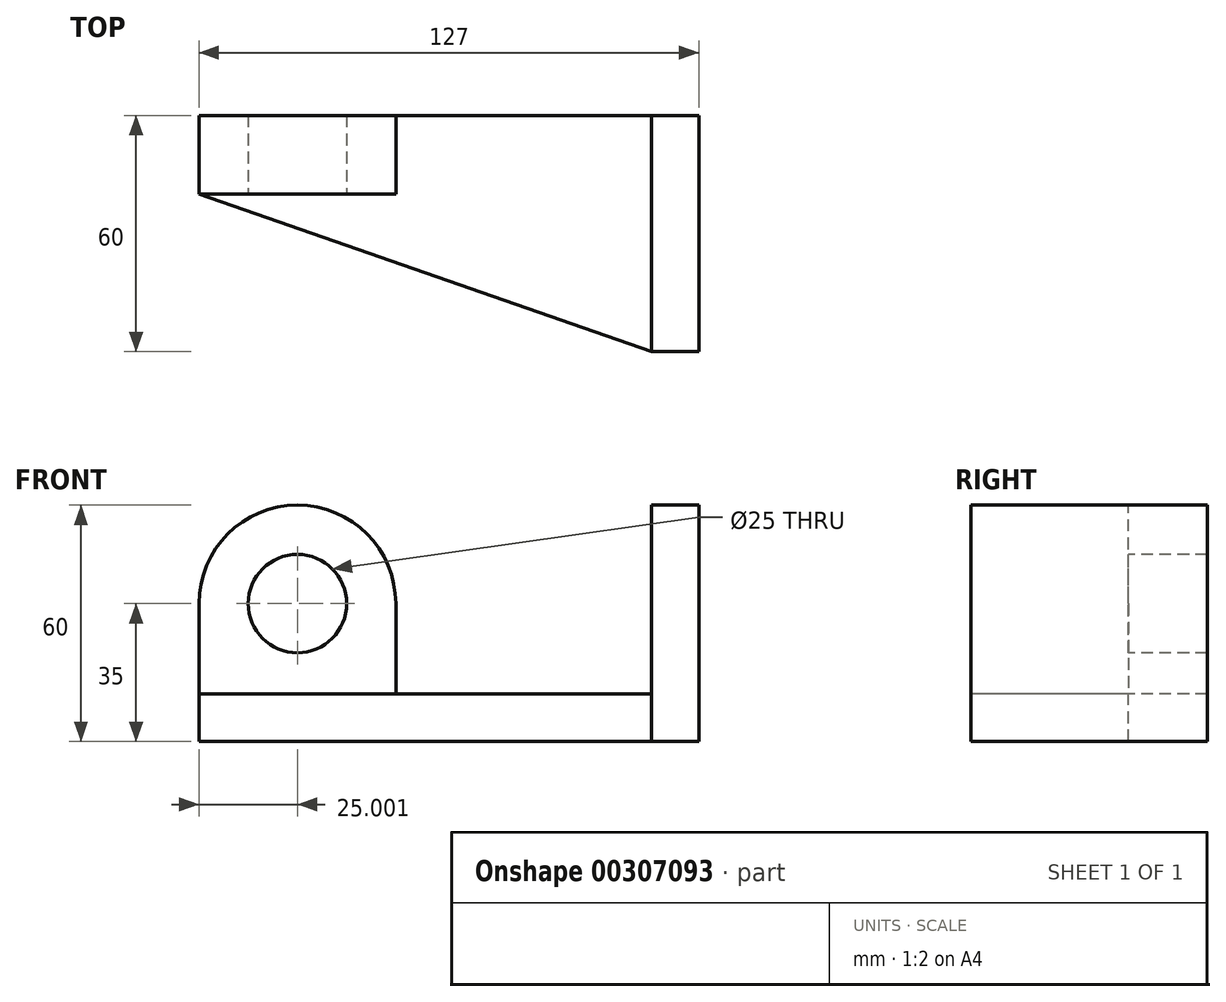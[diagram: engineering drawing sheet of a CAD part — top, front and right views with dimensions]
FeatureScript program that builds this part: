
annotation { "Feature Type Name" : "Feature", "Feature Type Description" : "" }
export const myFeature = defineFeature(function(context is Context, id is Id, definition is map)
    precondition{}
    {
        {
            var Q0;
            Q0=qCreatedBy(makeId("Top.planeOp"),FACE);
            var sketch = newSketch(context, id + "F0", { "sketchPlane" : qUnion([Q0])});
            skLineSegment(sketch, "E0.bottom", {"start": v(-57.94, 26.08) * mm, "end": v(57.06, 26.08) * mm});
            skLineSegment(sketch, "E0.top", {"start": v(-57.94, -33.92) * mm, "end": v(57.06, -33.92) * mm});
            skLineSegment(sketch, "E0.left", {"start": v(-57.94, 26.08) * mm, "end": v(-57.94, -33.92) * mm});
            skLineSegment(sketch, "E0.right", {"start": v(57.06, 26.08) * mm, "end": v(57.06, -33.92) * mm});
            skLineSegment(sketch, "E1.bottom", {"start": v(57.06, 26.08) * mm, "end": v(69.06, 26.08) * mm});
            skLineSegment(sketch, "E1.top", {"start": v(57.06, -33.92) * mm, "end": v(69.06, -33.92) * mm});
            skLineSegment(sketch, "E1.right", {"start": v(69.06, 26.08) * mm, "end": v(69.06, -33.92) * mm});
            skSolve(sketch);
        }
        {
            var Q0;
            Q0=makeQuery(id+"F0.imprint","IMPRINT",FACE,{"disambiguationData":[TD([[makeQuery(id+"F0.imprint","IMPRINT",EDGE,{"derivedFrom":sQuery(id+"F0.wireOp",EDGE,"E0.bottom")}),-1.0]])]});
            extrude(context, id + "F1", {"entities" : qUnion([Q0]), "depth" : 12 * mm});
        }
        {
            var Q0;
            Q0=makeQuery(id+"F0.imprint","IMPRINT",FACE,{"disambiguationData":[TD([[makeQuery(id+"F0.imprint","IMPRINT",EDGE,{"derivedFrom":sQuery(id+"F0.wireOp",EDGE,"E1.bottom")}),-1.0]])]});
            extrude(context, id + "F2", {"entities" : qUnion([Q0]), "operationType" : NewBodyOperationType.ADD, "depth" : 60 * mm});
        }
        {
            var Q0;
            Q0=makeQuery(id+"F1.opExtrude","CAP_FACE",FACE,{"disambiguationData":[OSD([sQuery(id+"F0.wireOp",EDGE,"E0.bottom"),sQuery(id+"F0.wireOp",EDGE,"E0.top"),sQuery(id+"F0.wireOp",EDGE,"E0.left"),sQuery(id+"F0.wireOp",EDGE,"E0.right")])],"isStart":false});
            var sketch = newSketch(context, id + "F3", { "sketchPlane" : qUnion([Q0])});
            skLineSegment(sketch, "E2", {"start": v(-57.94, 26.08) * mm, "end": v(-57.94, 6.08) * mm});
            skLineSegment(sketch, "E3", {"start": v(-57.94, 6.08) * mm, "end": v(57.06, -33.92) * mm});
            skLineSegment(sketch, "E4", {"start": v(57.06, -33.92) * mm, "end": v(-57.94, -33.92) * mm});
            skLineSegment(sketch, "E5", {"start": v(-57.94, -33.92) * mm, "end": v(-57.94, 6.08) * mm});
            skSolve(sketch);
        }
        {
            var Q0;
            Q0=makeQuery(id+"F3.imprint","IMPRINT",FACE,{"disambiguationData":[TD([[makeQuery(id+"F3.imprint","IMPRINT",EDGE,{"derivedFrom":sQuery(id+"F3.wireOp",EDGE,"E3")}),-1.0]])]});
            extrude(context, id + "F4", {"entities" : qUnion([Q0]), "operationType" : NewBodyOperationType.REMOVE, "oppositeDirection" : true, "depth" : 25 * mm});
        }
        {
            var Q0;
            Q0=makeQuery(id+"F1.opExtrude","CAP_FACE",FACE,{"disambiguationData":[OSD([sQuery(id+"F0.wireOp",EDGE,"E0.bottom"),sQuery(id+"F0.wireOp",EDGE,"E0.top"),sQuery(id+"F0.wireOp",EDGE,"E0.left"),sQuery(id+"F0.wireOp",EDGE,"E0.right")])],"isStart":false});
            var sketch = newSketch(context, id + "F5", { "sketchPlane" : qUnion([Q0])});
            skLineSegment(sketch, "E6.bottom", {"start": v(-57.94, 26.08) * mm, "end": v(-57.94, 26.08) * mm});
            skLineSegment(sketch, "E6.top", {"start": v(-57.94, 6.08) * mm, "end": v(-57.94, 6.08) * mm});
            skLineSegment(sketch, "E6.left", {"start": v(-57.94, 26.08) * mm, "end": v(-57.94, 6.08) * mm});
            skLineSegment(sketch, "E6.right", {"start": v(-57.94, 26.08) * mm, "end": v(-57.94, 6.08) * mm});
            skLineSegment(sketch, "E7.bottom", {"start": v(-57.94, 26.08) * mm, "end": v(-7.94, 26.08) * mm});
            skLineSegment(sketch, "E7.top", {"start": v(-57.94, 6.08) * mm, "end": v(-7.94, 6.08) * mm});
            skLineSegment(sketch, "E7.right", {"start": v(-7.94, 26.08) * mm, "end": v(-7.94, 6.08) * mm});
            skSolve(sketch);
        }
        {
            var Q0;
            Q0=makeQuery(id+"F5.imprint","IMPRINT",FACE,{"disambiguationData":[TD([[makeQuery(id+"F5.imprint","IMPRINT",EDGE,{"derivedFrom":sQuery(id+"F5.wireOp",EDGE,"E7.bottom")}),-1.0]])]});
            extrude(context, id + "F6", {"entities" : qUnion([Q0]), "operationType" : NewBodyOperationType.ADD, "depth" : 48 * mm});
        }
        {
            var Q0;
            Q0=makeQuery(id+"F6.opExtrude","SWEPT_FACE",FACE,{"disambiguationData":[OSD([sQuery(id+"F5.wireOp",EDGE,"E7.top")])]});
            var sketch = newSketch(context, id + "F7", { "sketchPlane" : qUnion([Q0])});
            skLineSegment(sketch, "E8", {"start": v(-57.94, 12) * mm, "end": v(-57.94, 35) * mm});
            skArc(sketch, "E9", {"start": v(-7.94, 35) * mm, "mid": v(-32.94, 60) * mm, "end": v(-57.94, 35) * mm});
            skPoint(sketch, "E9.centerSnap0", {"position": v(-32.94, 60) * mm});
            skLineSegment(sketch, "E10", {"start": v(-57.94, 35) * mm, "end": v(-7.94, 35) * mm});
            skSolve(sketch);
        }
        {
            var Q0;
            {var subQ0=sQuery(id+"F7.wireOp",EDGE,"E9");var subQ1=sQuery(id+"F5.wireOp",EDGE,"E7.top");var subQ4=makeQuery(id+"F6.opExtrude","CAP_EDGE",EDGE,{"disambiguationData":[OSD([subQ1])],"isStart":false});var subQ5=makeQuery(id+"F7.imprint","INTERSECT",VERTEX,{"derivedFrom":[subQ4,subQ0]});Q0=makeQuery(id+"F7.imprint","IMPRINT",FACE,{"disambiguationData":[TD([[makeQuery(id+"F7.imprint","IMPRINT",EDGE,{"disambiguationData":[TD([[subQ5,1.0]])],"derivedFrom":subQ4}),-1.0]])]});}
            var Q1;
            {var subQ0=sQuery(id+"F7.wireOp",EDGE,"E9");var subQ1=sQuery(id+"F5.wireOp",EDGE,"E7.top");var subQ4=makeQuery(id+"F6.opExtrude","CAP_EDGE",EDGE,{"disambiguationData":[OSD([subQ1])],"isStart":false});var subQ5=makeQuery(id+"F7.imprint","INTERSECT",VERTEX,{"derivedFrom":[subQ4,subQ0]});Q1=makeQuery(id+"F7.imprint","IMPRINT",FACE,{"disambiguationData":[TD([[makeQuery(id+"F7.imprint","IMPRINT",EDGE,{"disambiguationData":[TD([[subQ5,-1.0]])],"derivedFrom":subQ4}),-1.0]])]});}
            extrude(context, id + "F8", {"entities" : qUnion([Q0, Q1]), "operationType" : NewBodyOperationType.REMOVE, "oppositeDirection" : true, "depth" : 25 * mm});
        }
        {
            var Q0;
            Q0=makeQuery(id+"F6.opExtrude","SWEPT_FACE",FACE,{"disambiguationData":[OSD([sQuery(id+"F5.wireOp",EDGE,"E7.top")])]});
            var sketch = newSketch(context, id + "F9", { "sketchPlane" : qUnion([Q0])});
            skCircle(sketch, "E11", {"center": v(-32.94, 35) * mm, "radius": 12.5 * mm});
            skSolve(sketch);
        }
        {
            var Q0;
            Q0=makeQuery(id+"F9.imprint","IMPRINT",FACE,{"disambiguationData":[TD([[makeQuery(id+"F9.imprint","IMPRINT",EDGE,{"derivedFrom":sQuery(id+"F9.wireOp",EDGE,"E11")}),1.0]])]});
            extrude(context, id + "F10", {"entities" : qUnion([Q0]), "operationType" : NewBodyOperationType.REMOVE, "oppositeDirection" : true, "depth" : 25 * mm});
        }
    });
